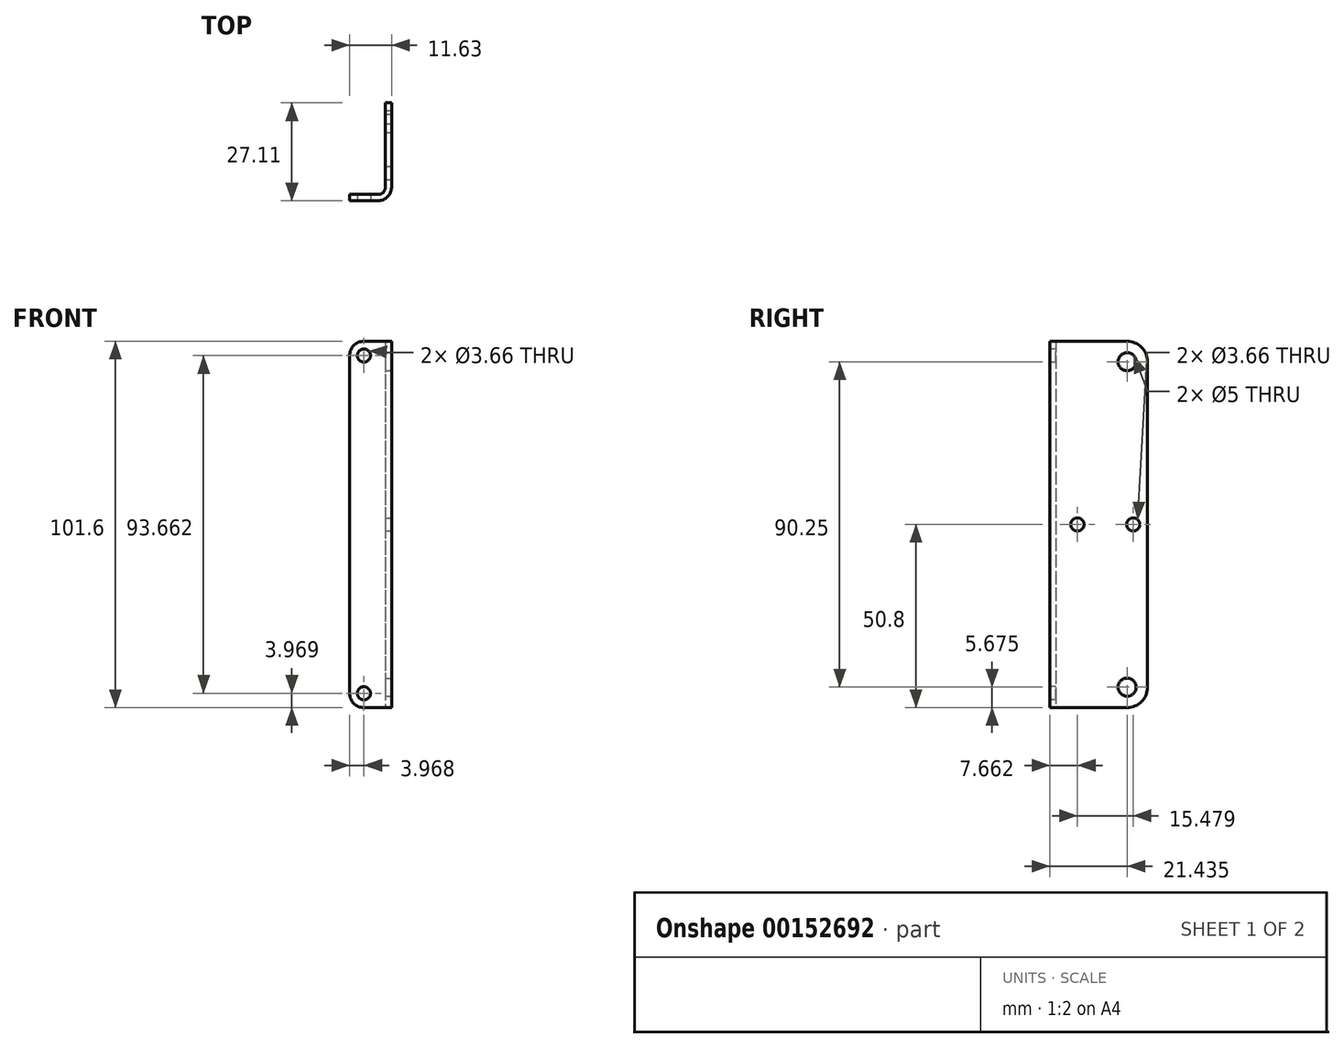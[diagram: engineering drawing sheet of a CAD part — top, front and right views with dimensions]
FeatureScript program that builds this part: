
annotation { "Feature Type Name" : "Feature", "Feature Type Description" : "" }
export const myFeature = defineFeature(function(context is Context, id is Id, definition is map)
    precondition{}
    {
        {
            var Q0;
            Q0=qCreatedBy(makeId("Top.planeOp"),FACE);
            var sketch = newSketch(context, id + "F0", { "sketchPlane" : qUnion([Q0])});
            skLineSegment(sketch, "E0.bottom", {"start": v(0, 0) * mm, "end": v(-9.92, 0) * mm});
            skLineSegment(sketch, "E0.top", {"start": v(1.7, -1.7) * mm, "end": v(-9.92, -1.7) * mm});
            skLineSegment(sketch, "E1.right", {"start": v(-9.92, -1.7) * mm, "end": v(-9.92, 0) * mm});
            skLineSegment(sketch, "E2.top", {"start": v(0, 25.4) * mm, "end": v(1.7, 25.4) * mm});
            skLineSegment(sketch, "E2.left", {"start": v(0, 0) * mm, "end": v(0, 25.4) * mm});
            skLineSegment(sketch, "E2.right", {"start": v(1.7, -1.7) * mm, "end": v(1.7, 25.4) * mm});
            skSolve(sketch);
        }
        {
            var Q0;
            Q0=qSketchRegion(id+"F0",true);
            extrude(context, id + "F1", {"entities" : qUnion([Q0]), "depth" : 101.6 * mm});
        }
        {
            var Q0;
            Q0=makeQuery(id+"F1.opExtrude","SWEPT_EDGE",EDGE,{"disambiguationData":[OSD([sQuery(id+"F0.wireOp",EDGE,"E0.top"),sQuery(id+"F0.wireOp",EDGE,"E2.right")])]});
            fillet(context, id + "F2", {"entities" : qUnion([Q0]), "radius" : 3.7 * mm, "tangentPropagation" : true, "allowEdgeOverflow" : false});
        }
        {
            var Q0;
            Q0=makeQuery(id+"F1.opExtrude","SWEPT_EDGE",EDGE,{"disambiguationData":[OSD([sQuery(id+"F0.wireOp",EDGE,"E0.bottom"),sQuery(id+"F0.wireOp",EDGE,"E2.left")])]});
            fillet(context, id + "F3", {"entities" : qUnion([Q0]), "radius" : 1.98 * mm, "tangentPropagation" : true, "allowEdgeOverflow" : false});
        }
        {
            var Q0;
            Q0=makeQuery(id+"F1.opExtrude","SWEPT_FACE",FACE,{"disambiguationData":[OSD([sQuery(id+"F0.wireOp",EDGE,"E2.right")])]});
            var sketch = newSketch(context, id + "F4", { "sketchPlane" : qUnion([Q0])});
            skLineSegment(sketch, "E3", {"start": v(25.4, 50.8) * mm, "end": v(21.43, 50.8) * mm, "construction": true});
            skLineSegment(sketch, "E4", {"start": v(21.43, 50.8) * mm, "end": v(5.95, 50.8) * mm, "construction": true});
            skLineSegment(sketch, "E5", {"start": v(5.95, 50.8) * mm, "end": v(1.98, 50.8) * mm, "construction": true});
            skCircle(sketch, "E6", {"center": v(21.43, 50.8) * mm, "radius": 1.83 * mm});
            skCircle(sketch, "E7", {"center": v(5.95, 50.8) * mm, "radius": 1.83 * mm});
            skLineSegment(sketch, "E8.bottom", {"start": v(25.4, 0) * mm, "end": v(19.72, 0) * mm, "construction": true});
            skLineSegment(sketch, "E8.top", {"start": v(25.4, 5.68) * mm, "end": v(19.72, 5.68) * mm, "construction": true});
            skLineSegment(sketch, "E8.left", {"start": v(25.4, 0) * mm, "end": v(25.4, 5.68) * mm, "construction": true});
            skLineSegment(sketch, "E8.right", {"start": v(19.72, 0) * mm, "end": v(19.72, 5.68) * mm, "construction": true});
            skLineSegment(sketch, "E9.bottom", {"start": v(25.4, 101.6) * mm, "end": v(19.72, 101.6) * mm, "construction": true});
            skLineSegment(sketch, "E9.top", {"start": v(25.4, 95.93) * mm, "end": v(19.72, 95.93) * mm, "construction": true});
            skLineSegment(sketch, "E9.left", {"start": v(25.4, 101.6) * mm, "end": v(25.4, 95.93) * mm, "construction": true});
            skLineSegment(sketch, "E9.right", {"start": v(19.72, 101.6) * mm, "end": v(19.72, 95.93) * mm, "construction": true});
            skCircle(sketch, "E10", {"center": v(19.72, 95.93) * mm, "radius": 2.5 * mm});
            skCircle(sketch, "E11", {"center": v(19.72, 5.68) * mm, "radius": 2.5 * mm});
            skSolve(sketch);
        }
        {
            var Q0;
            Q0 = qSketchRegion(id + "F4", true);
            var Q1;
            Q1=makeQuery(id+"F1.opExtrude","SWEPT_FACE",FACE,{"disambiguationData":[OSD([sQuery(id+"F0.wireOp",EDGE,"E2.left")])]});
            extrude(context, id + "F5", {"entities" : qUnion([Q0]), "operationType" : NewBodyOperationType.REMOVE, "endBound" : BoundingType.UP_TO_SURFACE, "oppositeDirection" : true, "endBoundEntityFace" : qUnion([Q1]), "depth" : 25.4 * mm});
        }
        {
            var Q0;
            Q0=makeQuery(id+"F1.opExtrude","CAP_EDGE",EDGE,{"disambiguationData":[OSD([sQuery(id+"F0.wireOp",EDGE,"E2.top")])],"isStart":false});
            var Q1;
            Q1=makeQuery(id+"F1.opExtrude","CAP_EDGE",EDGE,{"disambiguationData":[OSD([sQuery(id+"F0.wireOp",EDGE,"E2.top")])],"isStart":true});
            fillet(context, id + "F6", {"entities" : qUnion([Q0, Q1]), "radius" : 5.67 * mm, "tangentPropagation" : true, "allowEdgeOverflow" : false});
        }
        {
            var Q0;
            Q0=makeQuery(id+"F1.opExtrude","CAP_EDGE",EDGE,{"disambiguationData":[OSD([sQuery(id+"F0.wireOp",EDGE,"E1.right")])],"isStart":true});
            var Q1;
            Q1=makeQuery(id+"F1.opExtrude","CAP_EDGE",EDGE,{"disambiguationData":[OSD([sQuery(id+"F0.wireOp",EDGE,"E1.right")])],"isStart":false});
            fillet(context, id + "F7", {"entities" : qUnion([Q0, Q1]), "radius" : 3.97 * mm, "tangentPropagation" : true, "allowEdgeOverflow" : false});
        }
        {
            var Q0;
            Q0=makeQuery(id+"F1.opExtrude","SWEPT_FACE",FACE,{"disambiguationData":[OSD([sQuery(id+"F0.wireOp",EDGE,"E0.top")])]});
            var sketch = newSketch(context, id + "F8", { "sketchPlane" : qUnion([Q0])});
            skCircle(sketch, "E12", {"center": v(-5.95, 97.63) * mm, "radius": 1.83 * mm});
            skCircle(sketch, "E13", {"center": v(-5.95, 3.97) * mm, "radius": 1.83 * mm});
            skSolve(sketch);
        }
        {
            var Q0;
            Q0 = qSketchRegion(id + "F8", true);
            var Q1;
            Q1=makeQuery(id+"F1.opExtrude","SWEPT_FACE",FACE,{"disambiguationData":[OSD([sQuery(id+"F0.wireOp",EDGE,"E0.bottom")])]});
            extrude(context, id + "F9", {"entities" : qUnion([Q0]), "operationType" : NewBodyOperationType.REMOVE, "endBound" : BoundingType.UP_TO_SURFACE, "oppositeDirection" : true, "endBoundEntityFace" : qUnion([Q1]), "depth" : 25.4 * mm});
        }
    });
